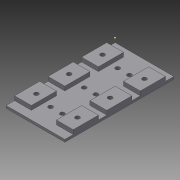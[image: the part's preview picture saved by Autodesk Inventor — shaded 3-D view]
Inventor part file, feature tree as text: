
AUTODESK INVENTOR PART (.ipt)
format: ipt  version: 2015 (Build 190159000, 159)  size: 188,928 bytes
history: native  units: mm
features: sketch x4, extrude x3
ambient origin geometry x8: Origin, YZ Plane, XZ Plane, XY Plane, X Axis, Y Axis, Z Axis, Center Point
bodies: Solid1 (feature_tree)
feature tree (7):
  extrude  "Extrusion1"  Depth=130.0mm
  extrude  "Extrusion3"  Depth=30.0mm
  sketch  "Sketch7"  dims[d4=20.0mm d5=30.0mm]
  extrude  "Extrusion4"  Depth=30.0mm
  sketch  "Sketch1"  dims[d0=70.0mm d1=130.0mm]
  sketch  "Sketch6"  dims[d2=20.0mm d3=30.0mm]
  sketch  "Sketch8"  dims[d6=20.0mm d7=30.0mm d8=20.0mm d9=30.0mm d10=20.0mm d11=30.0mm d12=20.0mm d13=30.0mm d14=10.0mm d15=10.0mm d16=10.0mm d17=10.0mm d18=10.0mm d19=0.0mm d20=30.0mm d21=3.0mm d22=0.0mm d27=8.0mm d28=0.0mm d29=5.2mm d30=5.2mm d31=5.2mm d32=5.2mm d33=5.2mm d34=5.2mm d35=5.2mm d36=5.2mm d37=5.2mm d38=5.2mm d39=5.2mm d40=5.2mm d41=15.0mm d42=10.0mm d43=8.0mm d44=8.0mm d45=15.0mm d46=10.0mm d47=15.0mm d48=15.0mm d49=8.0mm d50=8.0mm d51=0.0mm]
